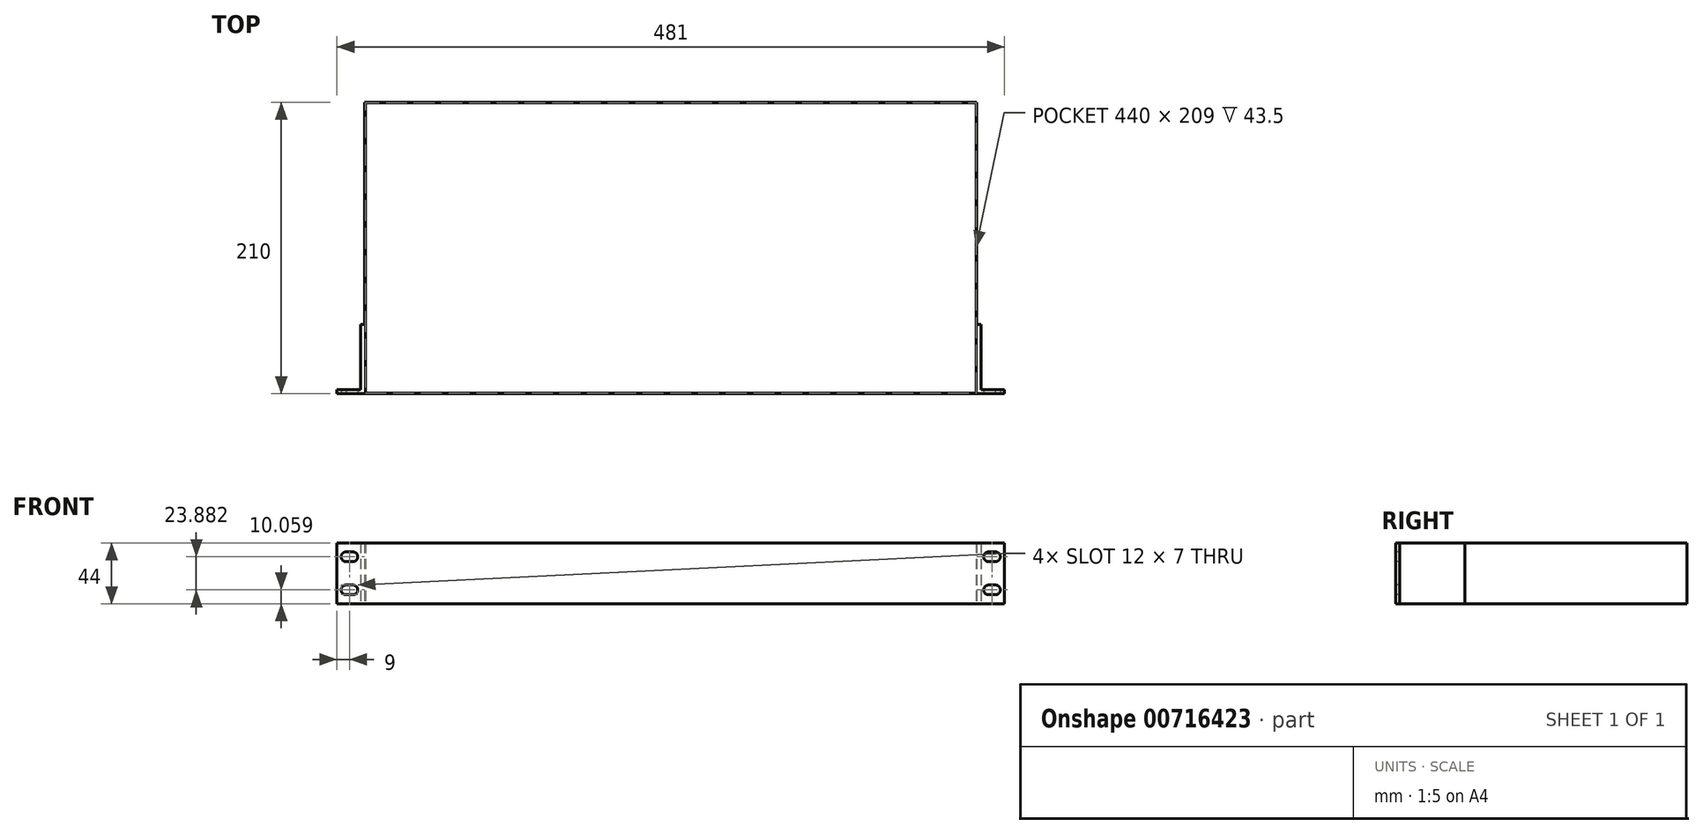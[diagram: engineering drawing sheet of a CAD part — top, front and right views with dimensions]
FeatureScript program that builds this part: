
annotation { "Feature Type Name" : "Feature", "Feature Type Description" : "" }
export const myFeature = defineFeature(function(context is Context, id is Id, definition is map)
    precondition{}
    {
        {
            var Q0;
            Q0=qCreatedBy(makeId("Top.planeOp"),FACE);
            var sketch = newSketch(context, id + "F0", { "sketchPlane" : qUnion([Q0])});
            skLineSegment(sketch, "E0.bottom", {"start": v(220.5, 105) * mm, "end": v(-220.5, 105) * mm});
            skLineSegment(sketch, "E0.top", {"start": v(220.5, -105) * mm, "end": v(-220.5, -105) * mm});
            skLineSegment(sketch, "E0.left", {"start": v(220.5, 105) * mm, "end": v(220.5, -105) * mm});
            skLineSegment(sketch, "E0.right", {"start": v(-220.5, 105) * mm, "end": v(-220.5, -105) * mm});
            skPoint(sketch, "E0.middle", {"position": v(0, 0) * mm});
            skSolve(sketch);
        }
        {
            var Q0;
            Q0 = qSketchRegion(id + "F0", true);
            extrude(context, id + "F1", {"entities" : qUnion([Q0]), "depth" : 44 * mm, "offsetDistance" : 25 * mm});
        }
        {
            var Q0;
            Q0=makeQuery(id+"F1.opExtrude","CAP_FACE",FACE,{"disambiguationData":[OSD([sQuery(id+"F0.wireOp",EDGE,"E0.bottom"),sQuery(id+"F0.wireOp",EDGE,"E0.top"),sQuery(id+"F0.wireOp",EDGE,"E0.left"),sQuery(id+"F0.wireOp",EDGE,"E0.right")])],"isStart":false});
            shell(context, id + "F2", {"entities" : qUnion([Q0]), "thickness" : 0.5 * mm});
        }
        {
            var Q0;
            Q0=makeQuery(id+"F1.opExtrude","CAP_FACE",FACE,{"disambiguationData":[OSD([sQuery(id+"F0.wireOp",EDGE,"E0.bottom"),sQuery(id+"F0.wireOp",EDGE,"E0.top"),sQuery(id+"F0.wireOp",EDGE,"E0.left"),sQuery(id+"F0.wireOp",EDGE,"E0.right")])],"isStart":true});
            var sketch = newSketch(context, id + "F3", { "sketchPlane" : qUnion([Q0])});
            skLineSegment(sketch, "E1", {"start": v(0, 105) * mm, "end": v(0, -105) * mm, "construction": true});
            skLineSegment(sketch, "E2", {"start": v(-220.5, 55) * mm, "end": v(-220.5, 105) * mm});
            skLineSegment(sketch, "E3", {"start": v(-220.5, 105) * mm, "end": v(-240.5, 105) * mm});
            skLineSegment(sketch, "E4.0", {"start": v(-223.5, 102) * mm, "end": v(-240.5, 102) * mm});
            skLineSegment(sketch, "E4.1", {"start": v(-223.5, 55) * mm, "end": v(-223.5, 102) * mm});
            skLineSegment(sketch, "E5", {"start": v(-240.5, 105) * mm, "end": v(-240.5, 102) * mm});
            skLineSegment(sketch, "E6", {"start": v(-223.5, 55) * mm, "end": v(-220.5, 55) * mm});
            skLineSegment(sketch, "E7.MirrorCS", {"start": v(223.5, 55) * mm, "end": v(220.5, 55) * mm});
            skLineSegment(sketch, "E8.MirrorCS", {"start": v(240.5, 105) * mm, "end": v(240.5, 102) * mm});
            skLineSegment(sketch, "E9.MirrorCS", {"start": v(220.5, 105) * mm, "end": v(240.5, 105) * mm});
            skLineSegment(sketch, "E10.MirrorCS", {"start": v(223.5, 102) * mm, "end": v(240.5, 102) * mm});
            skLineSegment(sketch, "E11.MirrorCS", {"start": v(223.5, 55) * mm, "end": v(223.5, 102) * mm});
            skLineSegment(sketch, "E12.MirrorCS", {"start": v(220.5, 55) * mm, "end": v(220.5, 105) * mm});
            skSolve(sketch);
        }
        {
            var Q0;
            Q0 = qSketchRegion(id + "F3", true);
            extrude(context, id + "F4", {"entities" : qUnion([Q0]), "oppositeDirection" : true, "depth" : 44 * mm, "offsetDistance" : 25 * mm});
        }
        {
            var Q0;
            Q0=makeQuery(id+"F4.opExtrude","SWEPT_BODY",BODY,{"disambiguationData":[OSD([sQuery(id+"F3.wireOp",EDGE,"E2"),sQuery(id+"F3.wireOp",EDGE,"E3"),sQuery(id+"F3.wireOp",EDGE,"E4.0"),sQuery(id+"F3.wireOp",EDGE,"E4.1"),sQuery(id+"F3.wireOp",EDGE,"E5"),sQuery(id+"F3.wireOp",EDGE,"E6")])]});
            var Q1;
            Q1=makeQuery(id+"F4.opExtrude","SWEPT_BODY",BODY,{"disambiguationData":[OSD([sQuery(id+"F3.wireOp",EDGE,"E7.MirrorCS"),sQuery(id+"F3.wireOp",EDGE,"E8.MirrorCS"),sQuery(id+"F3.wireOp",EDGE,"E9.MirrorCS"),sQuery(id+"F3.wireOp",EDGE,"E10.MirrorCS"),sQuery(id+"F3.wireOp",EDGE,"E11.MirrorCS"),sQuery(id+"F3.wireOp",EDGE,"E12.MirrorCS")])]});
            var Q2;
            Q2=makeQuery(id+"F1.opExtrude","SWEPT_BODY",BODY,{"disambiguationData":[OSD([sQuery(id+"F0.wireOp",EDGE,"E0.bottom"),sQuery(id+"F0.wireOp",EDGE,"E0.top"),sQuery(id+"F0.wireOp",EDGE,"E0.left"),sQuery(id+"F0.wireOp",EDGE,"E0.right")])]});
            booleanBodies(context, id + "F5", {"operationType" : BooleanOperationType.UNION, "tools" : qUnion([Q0, Q1, Q2])});
        }
        {
            var Q0;
            Q0=makeQuery(id+"F5.opBoolean","MERGE",FACE,{"derivedFrom":[makeQuery(id+"F1.opExtrude","SWEPT_FACE",FACE,{"disambiguationData":[OSD([sQuery(id+"F0.wireOp",EDGE,"E0.top")])]}),makeQuery(id+"F4.opExtrude","SWEPT_FACE",FACE,{"disambiguationData":[OSD([sQuery(id+"F3.wireOp",EDGE,"E3")])]}),makeQuery(id+"F4.opExtrude","SWEPT_FACE",FACE,{"disambiguationData":[OSD([sQuery(id+"F3.wireOp",EDGE,"E9.MirrorCS")])]})]});
            var sketch = newSketch(context, id + "F6", { "sketchPlane" : qUnion([Q0])});
            skLineSegment(sketch, "E13", {"start": v(-240.5, 22) * mm, "end": v(240.5, 22) * mm, "construction": true});
            skArc(sketch, "E14", {"start": v(-233.9, 37.44) * mm, "mid": v(-237.5, 33.98) * mm, "end": v(-233.97, 30.44) * mm});
            skArc(sketch, "E15", {"start": v(-229, 30.44) * mm, "mid": v(-225.5, 33.94) * mm, "end": v(-229, 37.44) * mm});
            skLineSegment(sketch, "E16", {"start": v(-234.11, 37.44) * mm, "end": v(-229, 37.44) * mm});
            skLineSegment(sketch, "E17", {"start": v(-233.97, 30.44) * mm, "end": v(-229, 30.44) * mm});
            skLineSegment(sketch, "E18.MirrorCS", {"start": v(-233.97, 13.56) * mm, "end": v(-229, 13.56) * mm});
            skLineSegment(sketch, "E19.MirrorCS", {"start": v(-234.11, 6.56) * mm, "end": v(-229, 6.56) * mm});
            skArc(sketch, "E20.MirrorCS", {"start": v(-229, 13.56) * mm, "mid": v(-225.5, 10.06) * mm, "end": v(-229, 6.56) * mm});
            skArc(sketch, "E21.MirrorCS", {"start": v(-233.9, 6.56) * mm, "mid": v(-237.5, 10.02) * mm, "end": v(-233.97, 13.56) * mm});
            skLineSegment(sketch, "E22", {"start": v(0, 44) * mm, "end": v(0, 0) * mm, "construction": true});
            skLineSegment(sketch, "E23.MirrorCS", {"start": v(234.11, 37.44) * mm, "end": v(229, 37.44) * mm});
            skLineSegment(sketch, "E24.MirrorCS", {"start": v(233.97, 30.44) * mm, "end": v(229, 30.44) * mm});
            skLineSegment(sketch, "E25.MirrorCS", {"start": v(233.97, 13.56) * mm, "end": v(229, 13.56) * mm});
            skLineSegment(sketch, "E26.MirrorCS", {"start": v(234.11, 6.56) * mm, "end": v(229, 6.56) * mm});
            skArc(sketch, "E27.MirrorCS", {"start": v(229, 30.44) * mm, "mid": v(225.5, 33.94) * mm, "end": v(229, 37.44) * mm});
            skArc(sketch, "E28.MirrorCS", {"start": v(229, 13.56) * mm, "mid": v(225.5, 10.06) * mm, "end": v(229, 6.56) * mm});
            skArc(sketch, "E29.MirrorCS", {"start": v(233.9, 37.44) * mm, "mid": v(237.5, 33.98) * mm, "end": v(233.97, 30.44) * mm});
            skArc(sketch, "E30.MirrorCS", {"start": v(233.9, 6.56) * mm, "mid": v(237.5, 10.02) * mm, "end": v(233.97, 13.56) * mm});
            skSolve(sketch);
        }
        {
            var Q0;
            Q0 = qSketchRegion(id + "F6", true);
            extrude(context, id + "F7", {"entities" : qUnion([Q0]), "operationType" : NewBodyOperationType.REMOVE, "oppositeDirection" : true, "depth" : 3 * mm, "offsetDistance" : 25 * mm});
        }
    });
